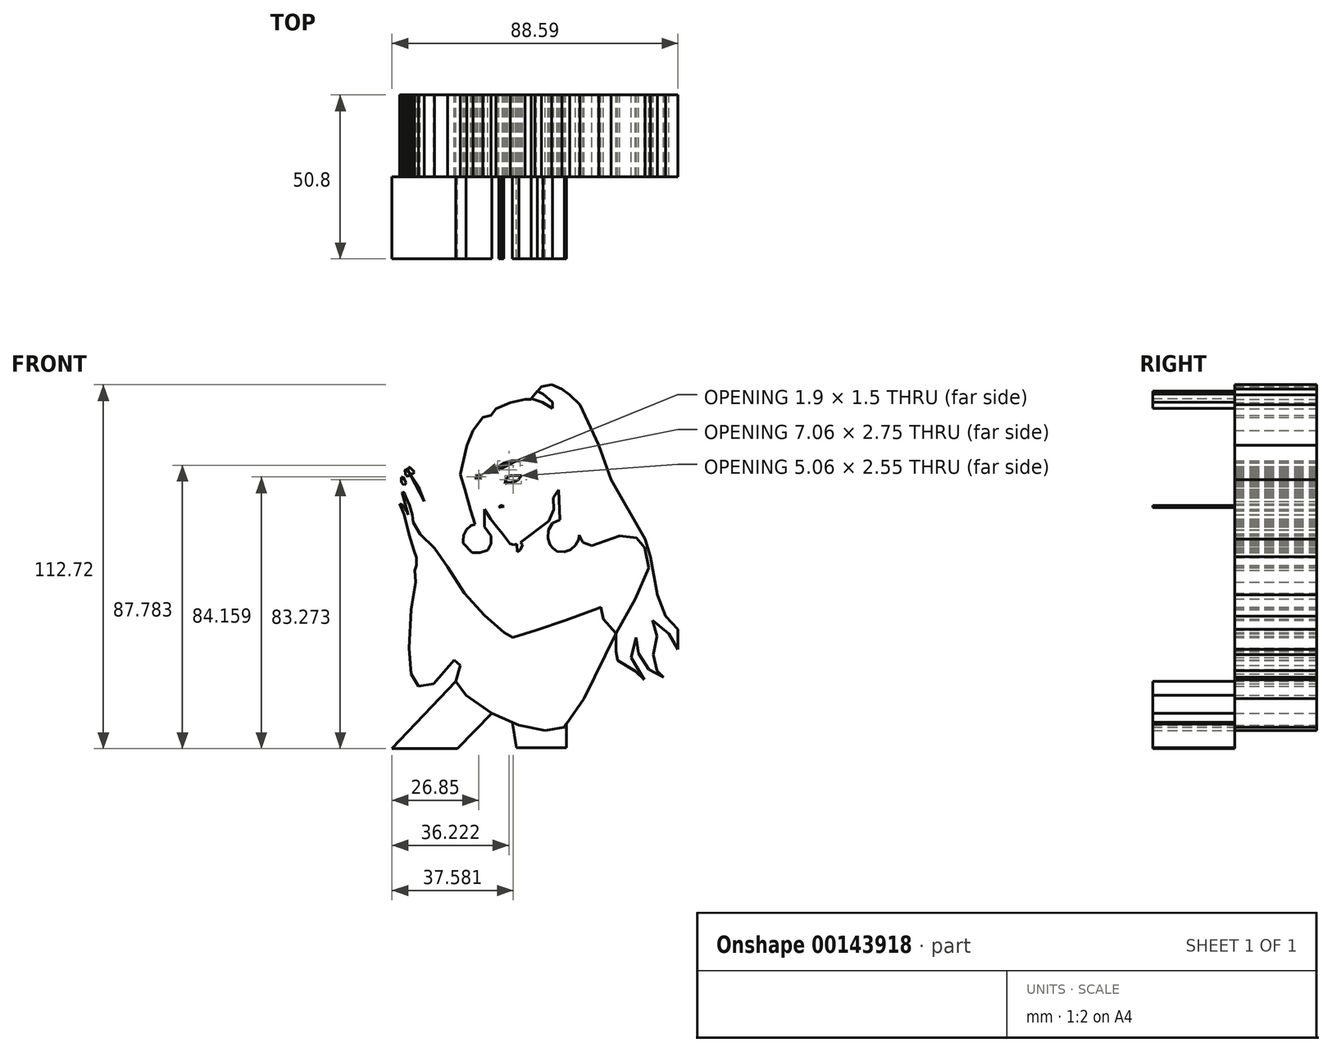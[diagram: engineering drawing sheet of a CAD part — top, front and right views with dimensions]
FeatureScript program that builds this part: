
annotation { "Feature Type Name" : "Feature", "Feature Type Description" : "" }
export const myFeature = defineFeature(function(context is Context, id is Id, definition is map)
    precondition{}
    {
        {
            var Q0;
            Q0=qCreatedBy(makeId("Front.planeOp"),FACE);
            var sketch = newSketch(context, id + "F0", { "sketchPlane" : qUnion([Q0])});
            skLineSegment(sketch, "E0", {"start": v(18.86, 2.45) * mm, "end": v(10.64, -3.42) * mm});
            skLineSegment(sketch, "E1", {"start": v(10.64, -3.42) * mm, "end": v(0.9, -7.18) * mm});
            skLineSegment(sketch, "E2", {"start": v(0.9, -7.18) * mm, "end": v(-4.27, -9.76) * mm});
            skLineSegment(sketch, "E3", {"start": v(-4.27, -9.76) * mm, "end": v(-10.84, -5.07) * mm});
            skLineSegment(sketch, "E4", {"start": v(-10.84, -5.07) * mm, "end": v(-17.53, 1.4) * mm});
            skLineSegment(sketch, "E5", {"start": v(-17.53, 1.4) * mm, "end": v(-24.1, 8.32) * mm});
            skLineSegment(sketch, "E6", {"start": v(-24.1, 8.32) * mm, "end": v(-25.63, 10.31) * mm});
            skLineSegment(sketch, "E7", {"start": v(-25.63, 10.31) * mm, "end": v(-25.63, 14.65) * mm});
            skLineSegment(sketch, "E8", {"start": v(-25.63, 14.65) * mm, "end": v(-27.16, 19.58) * mm});
            skLineSegment(sketch, "E9", {"start": v(-27.16, 19.58) * mm, "end": v(-28.21, 22.05) * mm});
            skLineSegment(sketch, "E10", {"start": v(-28.21, 22.05) * mm, "end": v(-28.21, 19.58) * mm});
            skLineSegment(sketch, "E11", {"start": v(-28.21, 19.58) * mm, "end": v(-27.07, 15.9) * mm});
            skLineSegment(sketch, "E12", {"start": v(-27.07, 15.9) * mm, "end": v(-28.21, 19.58) * mm});
            skLineSegment(sketch, "E13", {"start": v(-28.21, 19.58) * mm, "end": v(-32.09, 23.1) * mm});
            skLineSegment(sketch, "E14", {"start": v(-32.09, 23.1) * mm, "end": v(-36.08, 27.1) * mm});
            skLineSegment(sketch, "E15", {"start": v(30.24, -10.35) * mm, "end": v(20.73, -15.04) * mm});
            skLineSegment(sketch, "E16", {"start": v(20.73, -15.04) * mm, "end": v(10.64, -18.68) * mm});
            skLineSegment(sketch, "E17", {"start": v(10.64, -18.68) * mm, "end": v(1.7, -21.75) * mm});
            skLineSegment(sketch, "E18", {"start": v(1.7, -21.75) * mm, "end": v(-5.68, -24.05) * mm});
            skLineSegment(sketch, "E19", {"start": v(-5.68, -24.05) * mm, "end": v(-8.38, -22.56) * mm});
            skLineSegment(sketch, "E20", {"start": v(-8.38, -22.56) * mm, "end": v(-14.47, -17.16) * mm});
            skLineSegment(sketch, "E21", {"start": v(-14.47, -17.16) * mm, "end": v(-20.75, -10.33) * mm});
            skLineSegment(sketch, "E22", {"start": v(-20.75, -10.33) * mm, "end": v(-25.96, -2.28) * mm});
            skLineSegment(sketch, "E23", {"start": v(-25.96, -2.28) * mm, "end": v(-29.95, 3.6) * mm});
            skLineSegment(sketch, "E24", {"start": v(-29.95, 3.6) * mm, "end": v(-34.4, 7.97) * mm});
            skLineSegment(sketch, "E25", {"start": v(-34.4, 7.97) * mm, "end": v(-36.54, 11.65) * mm});
            skLineSegment(sketch, "E26", {"start": v(-28.55, 1.54) * mm, "end": v(-28.55, -3.51) * mm});
            skLineSegment(sketch, "E27", {"start": v(-28.55, -3.51) * mm, "end": v(-28.55, -14.12) * mm});
            skLineSegment(sketch, "E28", {"start": v(-28.55, -14.12) * mm, "end": v(-28.55, -20.51) * mm});
            skLineSegment(sketch, "E29", {"start": v(-28.55, -20.51) * mm, "end": v(-27.8, -29.5) * mm});
            skLineSegment(sketch, "E30", {"start": v(-28.55, -15.66) * mm, "end": v(-26.18, -10.8) * mm});
            skLineSegment(sketch, "E31", {"start": v(-26.18, -10.8) * mm, "end": v(-24.25, -4.93) * mm});
            skLineSegment(sketch, "E32", {"start": v(-40.74, 17.34) * mm, "end": v(-39.4, 14) * mm});
            skLineSegment(sketch, "E33", {"start": v(-39.4, 14) * mm, "end": v(-37.81, 7.82) * mm});
            skLineSegment(sketch, "E34", {"start": v(-37.81, 7.82) * mm, "end": v(-36.4, 2.8) * mm});
            skLineSegment(sketch, "E35", {"start": v(-36.4, 2.8) * mm, "end": v(-34.8, -1.46) * mm});
            skLineSegment(sketch, "E36", {"start": v(-35.6, 0.67) * mm, "end": v(-35.6, -1.68) * mm});
            skLineSegment(sketch, "E37", {"start": v(-35.6, -1.68) * mm, "end": v(-36.12, -3.2) * mm});
            skLineSegment(sketch, "E38", {"start": v(-36.12, -3.2) * mm, "end": v(-35.88, -6.96) * mm});
            skLineSegment(sketch, "E39", {"start": v(-35.88, -6.96) * mm, "end": v(-37.17, -15.36) * mm});
            skLineSegment(sketch, "E40", {"start": v(-37.17, -15.36) * mm, "end": v(-37.83, -27.34) * mm});
            skLineSegment(sketch, "E41", {"start": v(-37.83, -27.34) * mm, "end": v(-37.28, -35.34) * mm});
            skLineSegment(sketch, "E42", {"start": v(-37.28, -35.34) * mm, "end": v(-34.95, -39.15) * mm});
            skLineSegment(sketch, "E43", {"start": v(-34.95, -39.15) * mm, "end": v(-30.2, -38.45) * mm});
            skLineSegment(sketch, "E44", {"start": v(-30.2, -38.45) * mm, "end": v(-23.83, -31) * mm});
            skLineSegment(sketch, "E45", {"start": v(21.62, -14.6) * mm, "end": v(22.34, -18.4) * mm});
            skLineSegment(sketch, "E46", {"start": v(22.34, -18.4) * mm, "end": v(26.3, -22.78) * mm});
            skLineSegment(sketch, "E47", {"start": v(26.3, -22.78) * mm, "end": v(32.2, -12.1) * mm});
            skLineSegment(sketch, "E48", {"start": v(32.2, -12.1) * mm, "end": v(36.48, -2.41) * mm});
            skLineSegment(sketch, "E49", {"start": v(36.48, -2.41) * mm, "end": v(35.22, 3.73) * mm});
            skLineSegment(sketch, "E50", {"start": v(35.22, 3.73) * mm, "end": v(32.61, 6.76) * mm});
            skLineSegment(sketch, "E51", {"start": v(32.61, 6.76) * mm, "end": v(27.4, 7.44) * mm});
            skLineSegment(sketch, "E52", {"start": v(27.4, 7.44) * mm, "end": v(18.8, 4.4) * mm});
            skLineSegment(sketch, "E53", {"start": v(18.8, 4.4) * mm, "end": v(12.08, 2.39) * mm});
            skLineSegment(sketch, "E54", {"start": v(26.3, -22.78) * mm, "end": v(16.39, -43) * mm});
            skLineSegment(sketch, "E55", {"start": v(16.39, -43) * mm, "end": v(3.3, -37.77) * mm});
            skLineSegment(sketch, "E56", {"start": v(3.3, -37.77) * mm, "end": v(-6.56, -34.2) * mm});
            skLineSegment(sketch, "E57", {"start": v(-6.56, -34.2) * mm, "end": v(-15.48, -31) * mm});
            skLineSegment(sketch, "E58", {"start": v(16.39, -43) * mm, "end": v(10.24, -51.88) * mm});
            skLineSegment(sketch, "E59", {"start": v(10.24, -51.88) * mm, "end": v(4.3, -52.93) * mm});
            skLineSegment(sketch, "E60", {"start": v(4.3, -52.93) * mm, "end": v(-3.87, -51.22) * mm});
            skLineSegment(sketch, "E61", {"start": v(-3.87, -51.22) * mm, "end": v(-12.19, -47.52) * mm});
            skLineSegment(sketch, "E62", {"start": v(-12.19, -47.52) * mm, "end": v(-20.24, -41.98) * mm});
            skLineSegment(sketch, "E63", {"start": v(-20.24, -41.98) * mm, "end": v(-23.4, -37.63) * mm});
            skLineSegment(sketch, "E64", {"start": v(-23.4, -37.63) * mm, "end": v(-21.95, -32.74) * mm});
            skLineSegment(sketch, "E65", {"start": v(-23.4, -37.63) * mm, "end": v(-31.71, -46.2) * mm});
            skLineSegment(sketch, "E66", {"start": v(-31.71, -46.2) * mm, "end": v(-43.85, -58.08) * mm});
            skLineSegment(sketch, "E67", {"start": v(-12.19, -47.52) * mm, "end": v(-14.73, -51.21) * mm});
            skLineSegment(sketch, "E68", {"start": v(-14.73, -51.21) * mm, "end": v(-21.42, -56.76) * mm});
            skLineSegment(sketch, "E69", {"start": v(-21.42, -56.76) * mm, "end": v(-23, -58.34) * mm});
            skLineSegment(sketch, "E70", {"start": v(-5.82, -50.35) * mm, "end": v(-4.27, -55.3) * mm});
            skLineSegment(sketch, "E71", {"start": v(-4.27, -55.3) * mm, "end": v(-4.27, -58.6) * mm});
            skLineSegment(sketch, "E72", {"start": v(12.03, -49.29) * mm, "end": v(10.9, -58.6) * mm});
            skLineSegment(sketch, "E73", {"start": v(9.57, 20.9) * mm, "end": v(12, 14.2) * mm});
            skLineSegment(sketch, "E74", {"start": v(12, 14.2) * mm, "end": v(13.1, 10.76) * mm});
            skLineSegment(sketch, "E75", {"start": v(13.1, 10.76) * mm, "end": v(14.52, 8.33) * mm});
            skLineSegment(sketch, "E76", {"start": v(14.52, 8.33) * mm, "end": v(16.02, 5.4) * mm});
            skLineSegment(sketch, "E77", {"start": v(16.02, 5.4) * mm, "end": v(18.8, 4.4) * mm});
            skLineSegment(sketch, "E78", {"start": v(8.06, 21.15) * mm, "end": v(6.89, 19.23) * mm});
            skLineSegment(sketch, "E79", {"start": v(6.89, 19.23) * mm, "end": v(6.97, 15.54) * mm});
            skLineSegment(sketch, "E80", {"start": v(6.97, 15.54) * mm, "end": v(5.47, 12.02) * mm});
            skLineSegment(sketch, "E81", {"start": v(5.47, 12.02) * mm, "end": v(-3.33, 5.4) * mm});
            skLineSegment(sketch, "E82", {"start": v(-3.33, 5.4) * mm, "end": v(-4.4, 4.9) * mm});
            skLineSegment(sketch, "E83", {"start": v(-4.4, 4.9) * mm, "end": v(-5.5, 4.7) * mm});
            skLineSegment(sketch, "E84", {"start": v(-5.5, 4.7) * mm, "end": v(-6.68, 5.07) * mm});
            skLineSegment(sketch, "E85", {"start": v(-6.68, 5.07) * mm, "end": v(-7.41, 6.01) * mm});
            skLineSegment(sketch, "E86", {"start": v(-7.41, 6.01) * mm, "end": v(-8.89, 8.12) * mm});
            skLineSegment(sketch, "E87", {"start": v(-8.89, 8.12) * mm, "end": v(-10.62, 10.2) * mm});
            skLineSegment(sketch, "E88", {"start": v(-10.62, 10.2) * mm, "end": v(-12.65, 12.62) * mm});
            skLineSegment(sketch, "E89", {"start": v(-12.65, 12.62) * mm, "end": v(-14.56, 15.73) * mm});
            skLineSegment(sketch, "E90", {"start": v(-14.56, 15.73) * mm, "end": v(-15.45, 18.58) * mm});
            skLineSegment(sketch, "E91", {"start": v(-15.45, 18.58) * mm, "end": v(-15.45, 20.85) * mm});
            skLineSegment(sketch, "E92", {"start": v(-15.45, 20.85) * mm, "end": v(-16.92, 23.97) * mm});
            skLineSegment(sketch, "E93", {"start": v(-11.01, 36.98) * mm, "end": v(-13.12, 36.98) * mm});
            skLineSegment(sketch, "E94", {"start": v(-13.12, 36.98) * mm, "end": v(-14.77, 35.8) * mm});
            skLineSegment(sketch, "E95", {"start": v(-14.77, 35.8) * mm, "end": v(-15.87, 34.42) * mm});
            skLineSegment(sketch, "E96", {"start": v(-15.87, 34.42) * mm, "end": v(-16.55, 31.4) * mm});
            skLineSegment(sketch, "E97", {"start": v(-16.55, 31.4) * mm, "end": v(-17.24, 25.9) * mm});
            skLineSegment(sketch, "E98", {"start": v(-17.24, 25.9) * mm, "end": v(-17.24, 20.18) * mm});
            skLineSegment(sketch, "E99", {"start": v(-17.24, 20.18) * mm, "end": v(-16.74, 13.5) * mm});
            skLineSegment(sketch, "E100", {"start": v(-8.31, 37.21) * mm, "end": v(-5.89, 38.45) * mm});
            skLineSegment(sketch, "E101", {"start": v(-5.89, 38.45) * mm, "end": v(-2.73, 36.39) * mm});
            skLineSegment(sketch, "E102", {"start": v(-2.73, 36.39) * mm, "end": v(0.02, 32.45) * mm});
            skLineSegment(sketch, "E103", {"start": v(0.02, 32.45) * mm, "end": v(2.08, 27.42) * mm});
            skLineSegment(sketch, "E104", {"start": v(2.08, 27.42) * mm, "end": v(3, 21.92) * mm});
            skLineSegment(sketch, "E105", {"start": v(3, 21.92) * mm, "end": v(2.4, 17.34) * mm});
            skLineSegment(sketch, "E106", {"start": v(2.4, 17.34) * mm, "end": v(1.94, 13.45) * mm});
            skLineSegment(sketch, "E107", {"start": v(-3.33, 5.4) * mm, "end": v(-2.71, 4.58) * mm});
            skLineSegment(sketch, "E108", {"start": v(-2.71, 4.58) * mm, "end": v(-3.43, 3.03) * mm});
            skLineSegment(sketch, "E109", {"start": v(-3.43, 3.03) * mm, "end": v(-4.38, 2.5) * mm});
            skLineSegment(sketch, "E110", {"start": v(-4.38, 2.5) * mm, "end": v(-4.4, 4.9) * mm});
            skLineSegment(sketch, "E111", {"start": v(-4.38, 2.5) * mm, "end": v(-4.38, -0.87) * mm});
            skLineSegment(sketch, "E112", {"start": v(-4.38, -0.87) * mm, "end": v(-3.4, -4.34) * mm});
            skLineSegment(sketch, "E113", {"start": v(-3.4, -4.34) * mm, "end": v(-3.13, -6.75) * mm});
            skLineSegment(sketch, "E114", {"start": v(-23.07, -6.75) * mm, "end": v(-24.38, -11.78) * mm});
            skLineSegment(sketch, "E115", {"start": v(-24.38, -11.78) * mm, "end": v(-26.14, -16.59) * mm});
            skLineSegment(sketch, "E116", {"start": v(-26.14, -16.59) * mm, "end": v(-26.67, -23) * mm});
            skLineSegment(sketch, "E117", {"start": v(-26.67, -23) * mm, "end": v(-25.45, -27.97) * mm});
            skLineSegment(sketch, "E118", {"start": v(-25.45, -27.97) * mm, "end": v(-23.83, -31) * mm});
            skLineSegment(sketch, "E119", {"start": v(-23.83, -31) * mm, "end": v(-21.95, -32.74) * mm});
            skLineSegment(sketch, "E120", {"start": v(-21.95, -32.74) * mm, "end": v(-19.65, -38.05) * mm});
            skLineSegment(sketch, "E121", {"start": v(-19.65, -38.05) * mm, "end": v(-19.95, -39.04) * mm});
            skLineSegment(sketch, "E122", {"start": v(-19.95, -39.04) * mm, "end": v(-17.2, -36.06) * mm});
            skLineSegment(sketch, "E123", {"start": v(-17.2, -36.06) * mm, "end": v(-16.06, -33) * mm});
            skLineSegment(sketch, "E124", {"start": v(-16.06, -33) * mm, "end": v(-15.48, -31) * mm});
            skLineSegment(sketch, "E125", {"start": v(-15.48, -31) * mm, "end": v(-15.48, -27.2) * mm});
            skLineSegment(sketch, "E126", {"start": v(-15.48, -27.2) * mm, "end": v(-14.6, -23.46) * mm});
            skLineSegment(sketch, "E127", {"start": v(-14.6, -23.46) * mm, "end": v(-14.53, -22.32) * mm});
            skLineSegment(sketch, "E128", {"start": v(-14.53, -22.32) * mm, "end": v(-14.94, -16.64) * mm});
            skLineSegment(sketch, "E129", {"start": v(2.82, 38.96) * mm, "end": v(5.72, 34.85) * mm});
            skLineSegment(sketch, "E130", {"start": v(5.72, 34.85) * mm, "end": v(5.78, 30.48) * mm});
            skLineSegment(sketch, "E131", {"start": v(5.78, 30.48) * mm, "end": v(5.11, 23.15) * mm});
            skLineSegment(sketch, "E132", {"start": v(5.11, 23.15) * mm, "end": v(4.5, 17.96) * mm});
            skLineSegment(sketch, "E133", {"start": v(4.5, 17.96) * mm, "end": v(5.47, 12.02) * mm});
            skLineSegment(sketch, "E134", {"start": v(5.45, 26.81) * mm, "end": v(8.06, 25.9) * mm});
            skLineSegment(sketch, "E135", {"start": v(8.06, 25.9) * mm, "end": v(11.81, 25.9) * mm});
            skLineSegment(sketch, "E136", {"start": v(11.81, 25.9) * mm, "end": v(11.81, 28.47) * mm});
            skLineSegment(sketch, "E137", {"start": v(11.81, 28.47) * mm, "end": v(13.33, 31.38) * mm});
            skLineSegment(sketch, "E138", {"start": v(13.33, 31.38) * mm, "end": v(13.33, 36.87) * mm});
            skLineSegment(sketch, "E139", {"start": v(13.33, 36.87) * mm, "end": v(15.58, 32.5) * mm});
            skLineSegment(sketch, "E140", {"start": v(15.58, 32.5) * mm, "end": v(17.43, 29.6) * mm});
            skLineSegment(sketch, "E141", {"start": v(-6.78, 43.7) * mm, "end": v(-9.85, 45.56) * mm});
            skLineSegment(sketch, "E142", {"start": v(-9.85, 45.56) * mm, "end": v(-14.96, 44.07) * mm});
            skLineSegment(sketch, "E143", {"start": v(-14.96, 44.07) * mm, "end": v(-18.02, 40.08) * mm});
            skLineSegment(sketch, "E144", {"start": v(-18.02, 40.08) * mm, "end": v(-19.97, 35.34) * mm});
            skLineSegment(sketch, "E145", {"start": v(-19.97, 35.34) * mm, "end": v(-22.02, 26.52) * mm});
            skLineSegment(sketch, "E146", {"start": v(-22.02, 26.52) * mm, "end": v(-20.62, 21.96) * mm});
            skLineSegment(sketch, "E147", {"start": v(-20.62, 21.96) * mm, "end": v(-18.77, 15.46) * mm});
            skLineSegment(sketch, "E148", {"start": v(-18.77, 15.46) * mm, "end": v(-15.24, 3.76) * mm});
            skLineSegment(sketch, "E149", {"start": v(-15.24, 3.76) * mm, "end": v(-16.74, 13.5) * mm});
            skLineSegment(sketch, "E150", {"start": v(15.14, 48.07) * mm, "end": v(20.9, 35.53) * mm});
            skLineSegment(sketch, "E151", {"start": v(20.9, 35.53) * mm, "end": v(24.8, 24.84) * mm});
            skLineSegment(sketch, "E152", {"start": v(24.8, 24.84) * mm, "end": v(35.3, 6.45) * mm});
            skLineSegment(sketch, "E153", {"start": v(35.3, 6.45) * mm, "end": v(36.88, 0.97) * mm});
            skLineSegment(sketch, "E154", {"start": v(36.88, 0.97) * mm, "end": v(39.1, -10.83) * mm});
            skLineSegment(sketch, "E155", {"start": v(37.6, -18.7) * mm, "end": v(42.64, -22.92) * mm});
            skLineSegment(sketch, "E156", {"start": v(42.64, -22.92) * mm, "end": v(45.45, -27.72) * mm});
            skLineSegment(sketch, "E157", {"start": v(45.45, -27.72) * mm, "end": v(45.45, -21.51) * mm});
            skLineSegment(sketch, "E158", {"start": v(45.45, -21.51) * mm, "end": v(41.58, -17.41) * mm});
            skLineSegment(sketch, "E159", {"start": v(41.58, -17.41) * mm, "end": v(39.1, -10.83) * mm});
            skLineSegment(sketch, "E160", {"start": v(37.6, -18.7) * mm, "end": v(39, -23.74) * mm});
            skLineSegment(sketch, "E161", {"start": v(39, -23.74) * mm, "end": v(37.84, -29.36) * mm});
            skLineSegment(sketch, "E162", {"start": v(37.84, -29.36) * mm, "end": v(39, -34.4) * mm});
            skLineSegment(sketch, "E163", {"start": v(39, -34.4) * mm, "end": v(41, -36.38) * mm});
            skLineSegment(sketch, "E164", {"start": v(41, -36.38) * mm, "end": v(36.43, -33.92) * mm});
            skLineSegment(sketch, "E165", {"start": v(36.43, -33.92) * mm, "end": v(33.27, -29) * mm});
            skLineSegment(sketch, "E166", {"start": v(33.27, -29) * mm, "end": v(32.45, -24.09) * mm});
            skLineSegment(sketch, "E167", {"start": v(32.45, -24.09) * mm, "end": v(32.1, -18.23) * mm});
            skLineSegment(sketch, "E168", {"start": v(32.1, -18.23) * mm, "end": v(31.98, -15.54) * mm});
            skLineSegment(sketch, "E169", {"start": v(37.6, -18.7) * mm, "end": v(35.03, -15.42) * mm});
            skLineSegment(sketch, "E170", {"start": v(35.03, -15.42) * mm, "end": v(34.32, -11.8) * mm});
            skLineSegment(sketch, "E171", {"start": v(26.3, -22.78) * mm, "end": v(26.3, -28.42) * mm});
            skLineSegment(sketch, "E172", {"start": v(26.3, -28.42) * mm, "end": v(26.83, -31.23) * mm});
            skLineSegment(sketch, "E173", {"start": v(26.83, -31.23) * mm, "end": v(32.22, -34.51) * mm});
            skLineSegment(sketch, "E174", {"start": v(32.22, -34.51) * mm, "end": v(35.03, -37.09) * mm});
            skLineSegment(sketch, "E175", {"start": v(35.03, -37.09) * mm, "end": v(30.93, -30.3) * mm});
            skLineSegment(sketch, "E176", {"start": v(30.93, -30.3) * mm, "end": v(32.45, -24.09) * mm});
            skLineSegment(sketch, "E177", {"start": v(2.17, 49.78) * mm, "end": v(-1.89, 49.78) * mm});
            skLineSegment(sketch, "E178", {"start": v(-1.89, 49.78) * mm, "end": v(-6.43, 48.73) * mm});
            skLineSegment(sketch, "E179", {"start": v(-6.43, 48.73) * mm, "end": v(-10.97, 46.78) * mm});
            skLineSegment(sketch, "E180", {"start": v(-10.97, 46.78) * mm, "end": v(-12.4, 44.82) * mm});
            skLineSegment(sketch, "E181", {"start": v(2.17, 49.78) * mm, "end": v(6.06, 46.78) * mm});
            skLineSegment(sketch, "E182", {"start": v(6.06, 46.78) * mm, "end": v(11, 42.32) * mm});
            skLineSegment(sketch, "E183", {"start": v(11, 42.32) * mm, "end": v(13.33, 36.87) * mm});
            skLineSegment(sketch, "E184", {"start": v(0, 49.78) * mm, "end": v(1.08, 51.18) * mm});
            skLineSegment(sketch, "E185", {"start": v(1.08, 51.18) * mm, "end": v(3.46, 51.4) * mm});
            skLineSegment(sketch, "E186", {"start": v(3.46, 51.4) * mm, "end": v(6.14, 49.7) * mm});
            skLineSegment(sketch, "E187", {"start": v(6.14, 49.7) * mm, "end": v(6.55, 48.57) * mm});
            skLineSegment(sketch, "E188", {"start": v(6.55, 48.57) * mm, "end": v(5.98, 47.19) * mm});
            skLineSegment(sketch, "E189", {"start": v(5.98, 47.19) * mm, "end": v(6.06, 46.78) * mm});
            skLineSegment(sketch, "E190", {"start": v(1.08, 51.18) * mm, "end": v(3.14, 53.6) * mm});
            skLineSegment(sketch, "E191", {"start": v(3.14, 53.6) * mm, "end": v(6.38, 54.25) * mm});
            skLineSegment(sketch, "E192", {"start": v(6.38, 54.25) * mm, "end": v(9.47, 52.95) * mm});
            skLineSegment(sketch, "E193", {"start": v(9.47, 52.95) * mm, "end": v(11.9, 51.08) * mm});
            skLineSegment(sketch, "E194", {"start": v(11.9, 51.08) * mm, "end": v(15.14, 48.07) * mm});
            skLineSegment(sketch, "E195", {"start": v(13.1, 10.76) * mm, "end": v(10.92, 12.02) * mm});
            skLineSegment(sketch, "E196", {"start": v(10.92, 12.02) * mm, "end": v(8.88, 12.33) * mm});
            skLineSegment(sketch, "E197", {"start": v(8.88, 12.33) * mm, "end": v(6.64, 11.41) * mm});
            skLineSegment(sketch, "E198", {"start": v(6.64, 11.41) * mm, "end": v(5.27, 9.17) * mm});
            skLineSegment(sketch, "E199", {"start": v(5.27, 9.17) * mm, "end": v(5.22, 6.72) * mm});
            skLineSegment(sketch, "E200", {"start": v(5.22, 6.72) * mm, "end": v(5.87, 4.58) * mm});
            skLineSegment(sketch, "E201", {"start": v(5.87, 4.58) * mm, "end": v(6.69, 3.58) * mm});
            skLineSegment(sketch, "E202", {"start": v(6.69, 3.58) * mm, "end": v(7.99, 2.57) * mm});
            skLineSegment(sketch, "E203", {"start": v(7.99, 2.57) * mm, "end": v(10.31, 2.51) * mm});
            skLineSegment(sketch, "E204", {"start": v(10.31, 2.51) * mm, "end": v(12.17, 3.07) * mm});
            skLineSegment(sketch, "E205", {"start": v(12.17, 3.07) * mm, "end": v(13.7, 4.52) * mm});
            skLineSegment(sketch, "E206", {"start": v(13.7, 4.52) * mm, "end": v(14.67, 6.29) * mm});
            skLineSegment(sketch, "E207", {"start": v(14.67, 6.29) * mm, "end": v(14.86, 7.67) * mm});
            skLineSegment(sketch, "E208", {"start": v(-17.42, 10.98) * mm, "end": v(-18.69, 10.6) * mm});
            skLineSegment(sketch, "E209", {"start": v(-18.69, 10.6) * mm, "end": v(-20.03, 9.28) * mm});
            skLineSegment(sketch, "E210", {"start": v(-20.03, 9.28) * mm, "end": v(-20.93, 7.59) * mm});
            skLineSegment(sketch, "E211", {"start": v(-20.93, 7.59) * mm, "end": v(-21.13, 5.9) * mm});
            skLineSegment(sketch, "E212", {"start": v(-21.13, 5.9) * mm, "end": v(-21.13, 5.18) * mm});
            skLineSegment(sketch, "E213", {"start": v(-21.13, 5.18) * mm, "end": v(-21, 4.96) * mm});
            skLineSegment(sketch, "E214", {"start": v(-16.34, 10.96) * mm, "end": v(-14.52, 10.2) * mm});
            skLineSegment(sketch, "E215", {"start": v(-14.52, 10.2) * mm, "end": v(-12.5, 7.4) * mm});
            skLineSegment(sketch, "E216", {"start": v(-12.5, 7.4) * mm, "end": v(-12.5, 4.98) * mm});
            skLineSegment(sketch, "E217", {"start": v(-12.5, 4.98) * mm, "end": v(-13.5, 3) * mm});
            skLineSegment(sketch, "E218", {"start": v(-13.5, 3) * mm, "end": v(-15.88, 2.22) * mm});
            skLineSegment(sketch, "E219", {"start": v(-15.88, 2.22) * mm, "end": v(-18.32, 2.22) * mm});
            skLineSegment(sketch, "E220", {"start": v(-29.84, 18.18) * mm, "end": v(-32.99, 23.1) * mm});
            skLineSegment(sketch, "E221", {"start": v(-32.99, 23.1) * mm, "end": v(-36.08, 27.1) * mm});
            skLineSegment(sketch, "E222", {"start": v(-33.15, 18.1) * mm, "end": v(-34.98, 22.64) * mm});
            skLineSegment(sketch, "E223", {"start": v(-34.98, 22.64) * mm, "end": v(-37.77, 26.82) * mm});
            skLineSegment(sketch, "E224", {"start": v(-37.77, 26.82) * mm, "end": v(-35.98, 23.43) * mm});
            skLineSegment(sketch, "E225", {"start": v(-35.98, 23.43) * mm, "end": v(-33.15, 18.1) * mm});
            skLineSegment(sketch, "E226", {"start": v(-35.3, 16.5) * mm, "end": v(-38.8, 26.1) * mm});
            skLineSegment(sketch, "E227", {"start": v(-38.73, 23.83) * mm, "end": v(-35.3, 16.5) * mm});
            skLineSegment(sketch, "E228", {"start": v(-40, 23.11) * mm, "end": v(-38.88, 19.45) * mm});
            skLineSegment(sketch, "E229", {"start": v(-38.88, 19.45) * mm, "end": v(-37.73, 16.98) * mm});
            skLineSegment(sketch, "E230", {"start": v(-37.73, 16.98) * mm, "end": v(-36.85, 13.95) * mm});
            skLineSegment(sketch, "E231", {"start": v(-36.85, 13.95) * mm, "end": v(-36.54, 11.65) * mm});
            skLineSegment(sketch, "E232", {"start": v(-40.74, 17.34) * mm, "end": v(-39.8, 16.95) * mm});
            skLineSegment(sketch, "E233", {"start": v(-39.8, 16.95) * mm, "end": v(-38.62, 15.12) * mm});
            skLineSegment(sketch, "E234", {"start": v(-38.62, 15.12) * mm, "end": v(-37.04, 11.57) * mm});
            skLineSegment(sketch, "E235", {"start": v(-37.04, 11.57) * mm, "end": v(-36.45, 9.98) * mm});
            skLineSegment(sketch, "E236", {"start": v(-38.1, 13.96) * mm, "end": v(-39.76, 19.82) * mm});
            skLineSegment(sketch, "E237", {"start": v(-39.76, 19.82) * mm, "end": v(-40, 20.73) * mm});
            skLineSegment(sketch, "E238", {"start": v(-40, 20.73) * mm, "end": v(-39.86, 20.99) * mm});
            skLineSegment(sketch, "E239", {"start": v(-39.86, 20.99) * mm, "end": v(-39.5, 20.87) * mm});
            skLineSegment(sketch, "E240", {"start": v(-39.5, 20.87) * mm, "end": v(-39.28, 20.68) * mm});
            skLineSegment(sketch, "E241", {"start": v(-39.28, 20.68) * mm, "end": v(-39.07, 20.07) * mm});
            skLineSegment(sketch, "E242", {"start": v(-40, 23.11) * mm, "end": v(-40.27, 24.27) * mm});
            skLineSegment(sketch, "E243", {"start": v(-40.27, 24.27) * mm, "end": v(-40.3, 25.29) * mm});
            skLineSegment(sketch, "E244", {"start": v(-40.3, 25.29) * mm, "end": v(-40.15, 25.57) * mm});
            skLineSegment(sketch, "E245", {"start": v(-40.15, 25.57) * mm, "end": v(-39.9, 25.69) * mm});
            skLineSegment(sketch, "E246", {"start": v(-39.9, 25.69) * mm, "end": v(-39.6, 25.44) * mm});
            skLineSegment(sketch, "E247", {"start": v(-39.6, 25.44) * mm, "end": v(-39.24, 24.86) * mm});
            skLineSegment(sketch, "E248", {"start": v(-39.24, 24.86) * mm, "end": v(-38.97, 24.36) * mm});
            skLineSegment(sketch, "E249", {"start": v(-38.97, 24.36) * mm, "end": v(-38.8, 24.02) * mm});
            skLineSegment(sketch, "E250", {"start": v(-38.8, 24.02) * mm, "end": v(-38.73, 23.83) * mm});
            skLineSegment(sketch, "E251", {"start": v(-40.18, 23.91) * mm, "end": v(-39.79, 23.38) * mm});
            skLineSegment(sketch, "E252", {"start": v(-39.79, 23.38) * mm, "end": v(-39.39, 23.24) * mm});
            skLineSegment(sketch, "E253", {"start": v(-39.39, 23.24) * mm, "end": v(-38.96, 23.49) * mm});
            skLineSegment(sketch, "E254", {"start": v(-38.96, 23.49) * mm, "end": v(-38.92, 23.93) * mm});
            skLineSegment(sketch, "E255", {"start": v(-38.92, 23.93) * mm, "end": v(-38.97, 24.36) * mm});
            skLineSegment(sketch, "E256", {"start": v(-38.87, 28.1) * mm, "end": v(-39.12, 27.68) * mm});
            skLineSegment(sketch, "E257", {"start": v(-39.12, 27.68) * mm, "end": v(-39.03, 26.77) * mm});
            skLineSegment(sketch, "E258", {"start": v(-39.03, 26.77) * mm, "end": v(-38.8, 26.1) * mm});
            skLineSegment(sketch, "E259", {"start": v(-38.8, 26.1) * mm, "end": v(-38.48, 25.95) * mm});
            skLineSegment(sketch, "E260", {"start": v(-38.48, 25.95) * mm, "end": v(-38.1, 25.95) * mm});
            skLineSegment(sketch, "E261", {"start": v(-38.1, 25.95) * mm, "end": v(-37.9, 26.1) * mm});
            skLineSegment(sketch, "E262", {"start": v(-37.9, 26.1) * mm, "end": v(-37.75, 26.4) * mm});
            skLineSegment(sketch, "E263", {"start": v(-37.75, 26.4) * mm, "end": v(-37.77, 26.82) * mm});
            skLineSegment(sketch, "E264", {"start": v(-38.87, 28.1) * mm, "end": v(-38.64, 27.97) * mm});
            skLineSegment(sketch, "E265", {"start": v(-38.64, 27.97) * mm, "end": v(-38.3, 27.66) * mm});
            skLineSegment(sketch, "E266", {"start": v(-38.3, 27.66) * mm, "end": v(-38.06, 27.3) * mm});
            skLineSegment(sketch, "E267", {"start": v(-38.06, 27.3) * mm, "end": v(-37.77, 26.82) * mm});
            skLineSegment(sketch, "E268", {"start": v(-38.02, 28.58) * mm, "end": v(-38.12, 28.08) * mm});
            skLineSegment(sketch, "E269", {"start": v(-38.12, 28.08) * mm, "end": v(-37.94, 27.4) * mm});
            skLineSegment(sketch, "E270", {"start": v(-37.94, 27.4) * mm, "end": v(-37.63, 26.9) * mm});
            skLineSegment(sketch, "E271", {"start": v(-37.63, 26.9) * mm, "end": v(-37.26, 26.64) * mm});
            skLineSegment(sketch, "E272", {"start": v(-37.26, 26.64) * mm, "end": v(-36.74, 26.59) * mm});
            skLineSegment(sketch, "E273", {"start": v(-36.74, 26.59) * mm, "end": v(-36.41, 26.8) * mm});
            skLineSegment(sketch, "E274", {"start": v(-36.41, 26.8) * mm, "end": v(-36.21, 27.19) * mm});
            skLineSegment(sketch, "E275", {"start": v(-36.21, 27.19) * mm, "end": v(-36.93, 28.03) * mm});
            skLineSegment(sketch, "E276", {"start": v(-36.93, 28.03) * mm, "end": v(-37.63, 28.65) * mm});
            skLineSegment(sketch, "E277", {"start": v(-37.63, 28.65) * mm, "end": v(-37.94, 28.67) * mm});
            skLineSegment(sketch, "E278", {"start": v(-37.94, 28.67) * mm, "end": v(-38.02, 28.58) * mm});
            skLineSegment(sketch, "E279", {"start": v(-36.21, 27.19) * mm, "end": v(-36.08, 27.1) * mm});
            skLineSegment(sketch, "E280", {"start": v(-16.92, 23.97) * mm, "end": v(-17.24, 25.9) * mm});
            skLineSegment(sketch, "E281", {"start": v(1.94, 13.45) * mm, "end": v(4.5, 17.96) * mm});
            skLineSegment(sketch, "E282", {"start": v(11.81, 25.9) * mm, "end": v(10.84, 23.67) * mm});
            skLineSegment(sketch, "E283", {"start": v(10.84, 23.67) * mm, "end": v(9.89, 21.28) * mm});
            skLineSegment(sketch, "E284", {"start": v(9.89, 21.28) * mm, "end": v(9.57, 20.9) * mm});
            skLineSegment(sketch, "E285", {"start": v(9.24, 21.59) * mm, "end": v(8.98, 21.9) * mm});
            skLineSegment(sketch, "E286", {"start": v(8.98, 21.9) * mm, "end": v(8.47, 21.63) * mm});
            skLineSegment(sketch, "E287", {"start": v(8.47, 21.63) * mm, "end": v(8.88, 12.33) * mm});
            skLineSegment(sketch, "E288", {"start": v(9.24, 21.59) * mm, "end": v(8.88, 12.33) * mm});
            skLineSegment(sketch, "E289", {"start": v(9.57, 20.9) * mm, "end": v(9.22, 21.19) * mm});
            skLineSegment(sketch, "E290", {"start": v(9.22, 21.19) * mm, "end": v(9.24, 21.59) * mm});
            skLineSegment(sketch, "E291", {"start": v(8.06, 21.15) * mm, "end": v(8.47, 21.63) * mm});
            skLineSegment(sketch, "E292", {"start": v(-14.52, 10.2) * mm, "end": v(-14.56, 15.73) * mm});
            skLineSegment(sketch, "E293", {"start": v(-14.43, 10.26) * mm, "end": v(-14.12, 15.02) * mm});
            skLineSegment(sketch, "E294", {"start": v(-14.12, 15.02) * mm, "end": v(-14.56, 15.73) * mm});
            skLineSegment(sketch, "E295", {"start": v(-10.1, 27.94) * mm, "end": v(-8.06, 28.86) * mm});
            skLineSegment(sketch, "E296", {"start": v(-8.06, 28.86) * mm, "end": v(-4.9, 30.55) * mm});
            skLineSegment(sketch, "E297", {"start": v(-4.9, 30.55) * mm, "end": v(-3.39, 30.69) * mm});
            skLineSegment(sketch, "E298", {"start": v(-3.39, 30.69) * mm, "end": v(-6.11, 30.69) * mm});
            skLineSegment(sketch, "E299", {"start": v(-6.11, 30.69) * mm, "end": v(-8.21, 29.98) * mm});
            skLineSegment(sketch, "E300", {"start": v(-8.21, 29.98) * mm, "end": v(-10.31, 28.76) * mm});
            skLineSegment(sketch, "E301", {"start": v(-10.31, 28.76) * mm, "end": v(-10.45, 28.33) * mm});
            skLineSegment(sketch, "E302", {"start": v(-10.45, 28.33) * mm, "end": v(-10.1, 27.94) * mm});
            skLineSegment(sketch, "E303", {"start": v(-17.08, 24.94) * mm, "end": v(-16.47, 25.48) * mm});
            skLineSegment(sketch, "E304", {"start": v(-16.47, 25.48) * mm, "end": v(-15.43, 25.62) * mm});
            skLineSegment(sketch, "E305", {"start": v(-15.43, 25.62) * mm, "end": v(-15.34, 25.93) * mm});
            skLineSegment(sketch, "E306", {"start": v(-15.34, 25.93) * mm, "end": v(-15.72, 26.44) * mm});
            skLineSegment(sketch, "E307", {"start": v(-15.72, 26.44) * mm, "end": v(-16.56, 26.24) * mm});
            skLineSegment(sketch, "E308", {"start": v(-16.56, 26.24) * mm, "end": v(-17.24, 25.9) * mm});
            skLineSegment(sketch, "E309", {"start": v(-13.5, 24.48) * mm, "end": v(-12.32, 23.67) * mm});
            skLineSegment(sketch, "E310", {"start": v(-12.32, 23.67) * mm, "end": v(-12.45, 20) * mm});
            skLineSegment(sketch, "E311", {"start": v(-12.45, 20) * mm, "end": v(-12.66, 18.45) * mm});
            skLineSegment(sketch, "E312", {"start": v(-12.66, 18.45) * mm, "end": v(-12.85, 17.55) * mm});
            skLineSegment(sketch, "E313", {"start": v(-12.85, 17.55) * mm, "end": v(-12.66, 16.63) * mm});
            skLineSegment(sketch, "E314", {"start": v(-12.66, 16.63) * mm, "end": v(-12, 15.73) * mm});
            skLineSegment(sketch, "E315", {"start": v(-12, 15.73) * mm, "end": v(-11.12, 15.5) * mm});
            skLineSegment(sketch, "E316", {"start": v(-11.12, 15.5) * mm, "end": v(-10.4, 15.5) * mm});
            skLineSegment(sketch, "E317", {"start": v(-7.81, 16.23) * mm, "end": v(-7.35, 16.86) * mm});
            skLineSegment(sketch, "E318", {"start": v(-7.35, 16.86) * mm, "end": v(-7.72, 17.76) * mm});
            skLineSegment(sketch, "E319", {"start": v(-10.04, 16.14) * mm, "end": v(-9.39, 16.43) * mm});
            skLineSegment(sketch, "E320", {"start": v(-9.39, 16.43) * mm, "end": v(-8.73, 16.31) * mm});
            skLineSegment(sketch, "E321", {"start": v(-8.73, 16.31) * mm, "end": v(-8.5, 16.55) * mm});
            skLineSegment(sketch, "E322", {"start": v(-8.5, 16.55) * mm, "end": v(-8.65, 16.78) * mm});
            skLineSegment(sketch, "E323", {"start": v(-8.65, 16.78) * mm, "end": v(-9.3, 16.86) * mm});
            skLineSegment(sketch, "E324", {"start": v(-9.3, 16.86) * mm, "end": v(-9.93, 16.46) * mm});
            skLineSegment(sketch, "E325", {"start": v(-9.93, 16.46) * mm, "end": v(-10, 16.3) * mm});
            skLineSegment(sketch, "E326", {"start": v(-10, 16.3) * mm, "end": v(-10.05, 16.15) * mm});
            skLineSegment(sketch, "E327", {"start": v(-10.05, 16.15) * mm, "end": v(-10, 16.3) * mm});
            skLineSegment(sketch, "E328", {"start": v(-8.09, 23.53) * mm, "end": v(-7.51, 23.9) * mm});
            skLineSegment(sketch, "E329", {"start": v(-7.51, 23.9) * mm, "end": v(-6.48, 23.95) * mm});
            skLineSegment(sketch, "E330", {"start": v(-6.48, 23.95) * mm, "end": v(-4.85, 24.3) * mm});
            skLineSegment(sketch, "E331", {"start": v(-4.85, 24.3) * mm, "end": v(-3.93, 24.83) * mm});
            skLineSegment(sketch, "E332", {"start": v(-3.93, 24.83) * mm, "end": v(-3.03, 26.08) * mm});
            skLineSegment(sketch, "E333", {"start": v(-3.03, 26.08) * mm, "end": v(-4.11, 26.08) * mm});
            skLineSegment(sketch, "E334", {"start": v(-4.11, 26.08) * mm, "end": v(-6.35, 26.08) * mm});
            skLineSegment(sketch, "E335", {"start": v(-6.35, 26.08) * mm, "end": v(-7.23, 25.66) * mm});
            skLineSegment(sketch, "E336", {"start": v(-7.23, 25.66) * mm, "end": v(-7.87, 24.78) * mm});
            skLineSegment(sketch, "E337", {"start": v(-7.87, 24.78) * mm, "end": v(-8.09, 23.53) * mm});
            skLineSegment(sketch, "E338", {"start": v(-6, 26.08) * mm, "end": v(-6.37, 25.46) * mm});
            skLineSegment(sketch, "E339", {"start": v(-6.37, 25.46) * mm, "end": v(-6.24, 24.77) * mm});
            skLineSegment(sketch, "E340", {"start": v(-6.24, 24.77) * mm, "end": v(-5.5, 24.46) * mm});
            skLineSegment(sketch, "E341", {"start": v(-5.5, 24.46) * mm, "end": v(-4.83, 24.56) * mm});
            skLineSegment(sketch, "E342", {"start": v(-4.83, 24.56) * mm, "end": v(-4.26, 25.28) * mm});
            skLineSegment(sketch, "E343", {"start": v(-4.26, 25.28) * mm, "end": v(-4.4, 25.9) * mm});
            skLineSegment(sketch, "E344", {"start": v(-4.4, 25.9) * mm, "end": v(-4.57, 26.07) * mm});
            skLineSegment(sketch, "E345", {"start": v(-4.57, 26.07) * mm, "end": v(-4.11, 26.08) * mm});
            skSolve(sketch);
        }
        {
            var Q0;
            Q0 = qSketchRegion(id + "F0", true);
            extrude(context, id + "F1", {"entities" : qUnion([Q0]), "depth" : 25.4 * mm});
        }
        {
            var Q0;
            Q0=makeQuery(id+"F1.opExtrude","CAP_FACE",FACE,{"disambiguationData":[OSD([sQuery(id+"F0.wireOp",EDGE,"E15"),sQuery(id+"F0.wireOp",EDGE,"E16"),sQuery(id+"F0.wireOp",EDGE,"E17"),sQuery(id+"F0.wireOp",EDGE,"E18"),sQuery(id+"F0.wireOp",EDGE,"E19"),sQuery(id+"F0.wireOp",EDGE,"E20"),sQuery(id+"F0.wireOp",EDGE,"E21"),sQuery(id+"F0.wireOp",EDGE,"E22"),sQuery(id+"F0.wireOp",EDGE,"E23"),sQuery(id+"F0.wireOp",EDGE,"E24"),sQuery(id+"F0.wireOp",EDGE,"E25"),sQuery(id+"F0.wireOp",EDGE,"E32"),sQuery(id+"F0.wireOp",EDGE,"E33"),sQuery(id+"F0.wireOp",EDGE,"E34"),sQuery(id+"F0.wireOp",EDGE,"E35"),sQuery(id+"F0.wireOp",EDGE,"E36"),sQuery(id+"F0.wireOp",EDGE,"E37"),sQuery(id+"F0.wireOp",EDGE,"E38"),sQuery(id+"F0.wireOp",EDGE,"E39"),sQuery(id+"F0.wireOp",EDGE,"E40"),sQuery(id+"F0.wireOp",EDGE,"E41"),sQuery(id+"F0.wireOp",EDGE,"E42"),sQuery(id+"F0.wireOp",EDGE,"E43"),sQuery(id+"F0.wireOp",EDGE,"E44"),sQuery(id+"F0.wireOp",EDGE,"E45"),sQuery(id+"F0.wireOp",EDGE,"E46"),sQuery(id+"F0.wireOp",EDGE,"E54"),sQuery(id+"F0.wireOp",EDGE,"E58"),sQuery(id+"F0.wireOp",EDGE,"E59"),sQuery(id+"F0.wireOp",EDGE,"E60"),sQuery(id+"F0.wireOp",EDGE,"E61"),sQuery(id+"F0.wireOp",EDGE,"E62"),sQuery(id+"F0.wireOp",EDGE,"E63"),sQuery(id+"F0.wireOp",EDGE,"E64"),sQuery(id+"F0.wireOp",EDGE,"E119"),sQuery(id+"F0.wireOp",EDGE,"E228"),sQuery(id+"F0.wireOp",EDGE,"E229"),sQuery(id+"F0.wireOp",EDGE,"E230"),sQuery(id+"F0.wireOp",EDGE,"E231"),sQuery(id+"F0.wireOp",EDGE,"E232"),sQuery(id+"F0.wireOp",EDGE,"E233"),sQuery(id+"F0.wireOp",EDGE,"E234"),sQuery(id+"F0.wireOp",EDGE,"E236"),sQuery(id+"F0.wireOp",EDGE,"E237"),sQuery(id+"F0.wireOp",EDGE,"E238"),sQuery(id+"F0.wireOp",EDGE,"E239"),sQuery(id+"F0.wireOp",EDGE,"E240"),sQuery(id+"F0.wireOp",EDGE,"E241")])],"isStart":false});
            var sketch = newSketch(context, id + "F2", { "sketchPlane" : qUnion([Q0])});
            skLineSegment(sketch, "E346", {"start": v(21.62, -14.6) * mm, "end": v(31.15, -10.5) * mm});
            skLineSegment(sketch, "E347", {"start": v(18.9, 2.44) * mm, "end": v(9.54, -3.73) * mm});
            skLineSegment(sketch, "E348", {"start": v(9.54, -3.73) * mm, "end": v(-3.78, -9.66) * mm});
            skLineSegment(sketch, "E349", {"start": v(-3.78, -9.66) * mm, "end": v(-15.27, -0.99) * mm});
            skLineSegment(sketch, "E350", {"start": v(-15.27, -0.99) * mm, "end": v(-25.4, 9.67) * mm});
            skLineSegment(sketch, "E351", {"start": v(-25.4, 9.67) * mm, "end": v(-25.4, 14.23) * mm});
            skLineSegment(sketch, "E352", {"start": v(-25.4, 14.23) * mm, "end": v(-27, 19.1) * mm});
            skLineSegment(sketch, "E353", {"start": v(-27, 19.1) * mm, "end": v(-27.75, 20.17) * mm});
            skLineSegment(sketch, "E354", {"start": v(-27.75, 20.17) * mm, "end": v(-27.75, 18.57) * mm});
            skLineSegment(sketch, "E355", {"start": v(-27.75, 18.57) * mm, "end": v(-29.35, 20.47) * mm});
            skLineSegment(sketch, "E356", {"start": v(-29.35, 20.47) * mm, "end": v(-30.26, 21.57) * mm});
            skLineSegment(sketch, "E357", {"start": v(-30.26, 21.57) * mm, "end": v(-36.24, 27.23) * mm});
            skLineSegment(sketch, "E358", {"start": v(-36.24, 27.23) * mm, "end": v(-32.98, 23.47) * mm});
            skLineSegment(sketch, "E359", {"start": v(-32.98, 23.47) * mm, "end": v(-29.7, 17.68) * mm});
            skLineSegment(sketch, "E360", {"start": v(-38.8, 26.03) * mm, "end": v(-35.14, 16.38) * mm});
            skLineSegment(sketch, "E361", {"start": v(-35.14, 16.38) * mm, "end": v(-38.93, 24.2) * mm});
            skLineSegment(sketch, "E362", {"start": v(-40.16, 23.88) * mm, "end": v(-39.28, 20.68) * mm});
            skLineSegment(sketch, "E363", {"start": v(-23.4, -37.63) * mm, "end": v(-43.14, -58.47) * mm});
            skLineSegment(sketch, "E364", {"start": v(-43.14, -58.47) * mm, "end": v(-22.84, -58.47) * mm});
            skLineSegment(sketch, "E365", {"start": v(-22.84, -58.47) * mm, "end": v(-12.19, -47.52) * mm});
            skLineSegment(sketch, "E366", {"start": v(-12.19, -47.52) * mm, "end": v(-5.82, -50.35) * mm});
            skLineSegment(sketch, "E367", {"start": v(-5.82, -50.35) * mm, "end": v(-4.53, -58.2) * mm});
            skLineSegment(sketch, "E368", {"start": v(-4.53, -58.2) * mm, "end": v(10.95, -58.2) * mm});
            skLineSegment(sketch, "E369", {"start": v(10.95, -58.2) * mm, "end": v(10.95, -50.86) * mm});
            skLineSegment(sketch, "E370", {"start": v(16.39, -43) * mm, "end": v(-15.3, -31.13) * mm});
            skLineSegment(sketch, "E371", {"start": v(-15.3, -31.13) * mm, "end": v(-21.1, -28.85) * mm});
            skLineSegment(sketch, "E372", {"start": v(-21.1, -28.85) * mm, "end": v(-21.95, -32.74) * mm});
            skLineSegment(sketch, "E373", {"start": v(-17.58, 11) * mm, "end": v(-14.8, 9.96) * mm});
            skLineSegment(sketch, "E374", {"start": v(14.92, 7.25) * mm, "end": v(14.06, 9.96) * mm});
            skLineSegment(sketch, "E375", {"start": v(14.06, 9.96) * mm, "end": v(12.46, 11.18) * mm});
            skLineSegment(sketch, "E376", {"start": v(12.46, 11.18) * mm, "end": v(9.14, 12.66) * mm});
            skLineSegment(sketch, "E377", {"start": v(-4.32, 2.74) * mm, "end": v(-4.32, 0) * mm});
            skLineSegment(sketch, "E378", {"start": v(-4.32, 0) * mm, "end": v(-3.46, -4.59) * mm});
            skLineSegment(sketch, "E379", {"start": v(-3.46, -4.59) * mm, "end": v(-3.78, -9.66) * mm});
            skLineSegment(sketch, "E380", {"start": v(-28.44, 1.37) * mm, "end": v(-28.44, -16.24) * mm});
            skPoint(sketch, "E380.startSnap0", {"position": v(-4.32, 1.37) * mm});
            skLineSegment(sketch, "E381", {"start": v(-28.44, -16.24) * mm, "end": v(-24.26, -4.9) * mm});
            skLineSegment(sketch, "E382", {"start": v(-28.44, -16.24) * mm, "end": v(-27.7, -30.02) * mm});
            skLineSegment(sketch, "E383", {"start": v(8.64, 21.8) * mm, "end": v(11.53, 28.13) * mm});
            skLineSegment(sketch, "E384", {"start": v(11.53, 28.13) * mm, "end": v(13.85, 34.63) * mm});
            skLineSegment(sketch, "E385", {"start": v(13.85, 34.63) * mm, "end": v(12.65, 39.52) * mm});
            skLineSegment(sketch, "E386", {"start": v(0, 49.97) * mm, "end": v(3.42, 48.85) * mm});
            skLineSegment(sketch, "E387", {"start": v(3.42, 48.85) * mm, "end": v(6.6, 46.98) * mm});
            skLineSegment(sketch, "E388", {"start": v(6.6, 46.98) * mm, "end": v(9.58, 43.9) * mm});
            skLineSegment(sketch, "E389", {"start": v(9.58, 43.9) * mm, "end": v(12.65, 39.52) * mm});
            skLineSegment(sketch, "E390", {"start": v(6.6, 46.98) * mm, "end": v(6.6, 48.85) * mm});
            skLineSegment(sketch, "E391", {"start": v(6.6, 48.85) * mm, "end": v(3.6, 51.37) * mm});
            skLineSegment(sketch, "E392", {"start": v(3.6, 51.37) * mm, "end": v(1.92, 52.2) * mm});
            skLineSegment(sketch, "E393", {"start": v(1.92, 52.2) * mm, "end": v(0, 49.97) * mm});
            skLineSegment(sketch, "E394", {"start": v(-12.48, 22.8) * mm, "end": v(-14.1, 23.24) * mm});
            skLineSegment(sketch, "E395", {"start": v(-14.1, 23.24) * mm, "end": v(-15.86, 22.02) * mm});
            skLineSegment(sketch, "E396", {"start": v(-15.86, 22.02) * mm, "end": v(-15.42, 20.85) * mm});
            skLineSegment(sketch, "E397", {"start": v(-15.42, 20.85) * mm, "end": v(-14.1, 20.85) * mm});
            skLineSegment(sketch, "E398", {"start": v(-14.1, 20.85) * mm, "end": v(-12.52, 21.8) * mm});
            skLineSegment(sketch, "E399", {"start": v(-12.52, 21.8) * mm, "end": v(-12.48, 22.8) * mm});
            skLineSegment(sketch, "E400", {"start": v(-13.51, 24.3) * mm, "end": v(-12.45, 23.64) * mm});
            skLineSegment(sketch, "E401", {"start": v(-12.45, 23.64) * mm, "end": v(-12.26, 22.5) * mm});
            skLineSegment(sketch, "E402", {"start": v(-12.26, 22.5) * mm, "end": v(-12.48, 20.26) * mm});
            skLineSegment(sketch, "E403", {"start": v(-12.48, 20.26) * mm, "end": v(-12.7, 18.02) * mm});
            skLineSegment(sketch, "E404", {"start": v(-12.7, 18.02) * mm, "end": v(-12.85, 16.95) * mm});
            skLineSegment(sketch, "E405", {"start": v(-12.85, 16.95) * mm, "end": v(-12.2, 15.93) * mm});
            skLineSegment(sketch, "E406", {"start": v(-12.2, 15.93) * mm, "end": v(-11.27, 15.34) * mm});
            skLineSegment(sketch, "E407", {"start": v(-11.27, 15.34) * mm, "end": v(-10.28, 15.34) * mm});
            skLineSegment(sketch, "E408", {"start": v(-7.86, 17.76) * mm, "end": v(-7.3, 17.21) * mm});
            skLineSegment(sketch, "E409", {"start": v(-7.3, 17.21) * mm, "end": v(-7.67, 16.4) * mm});
            skLineSegment(sketch, "E410", {"start": v(-10.07, 16.18) * mm, "end": v(-9.34, 16.4) * mm});
            skLineSegment(sketch, "E411", {"start": v(-9.34, 16.4) * mm, "end": v(-8.73, 16.31) * mm});
            skLineSegment(sketch, "E412", {"start": v(-8.73, 16.31) * mm, "end": v(-8.55, 16.58) * mm});
            skLineSegment(sketch, "E413", {"start": v(-8.55, 16.58) * mm, "end": v(-8.94, 16.83) * mm});
            skLineSegment(sketch, "E414", {"start": v(-8.94, 16.83) * mm, "end": v(-9.5, 16.85) * mm});
            skLineSegment(sketch, "E415", {"start": v(-9.5, 16.85) * mm, "end": v(-10.07, 16.18) * mm});
            skLineSegment(sketch, "E416", {"start": v(-9.63, 11.74) * mm, "end": v(-8.83, 12.6) * mm});
            skLineSegment(sketch, "E417", {"start": v(-8.83, 12.6) * mm, "end": v(-7.53, 12.97) * mm});
            skLineSegment(sketch, "E418", {"start": v(-7.53, 12.97) * mm, "end": v(-4.8, 13.23) * mm});
            skLineSegment(sketch, "E419", {"start": v(-4.8, 13.23) * mm, "end": v(-5, 12.4) * mm});
            skLineSegment(sketch, "E420", {"start": v(-5, 12.4) * mm, "end": v(-6.36, 11.14) * mm});
            skLineSegment(sketch, "E421", {"start": v(-6.36, 11.14) * mm, "end": v(-8.52, 10.56) * mm});
            skLineSegment(sketch, "E422", {"start": v(-8.52, 10.56) * mm, "end": v(-9.63, 11.74) * mm});
            skLineSegment(sketch, "E423", {"start": v(-4.33, 13.51) * mm, "end": v(-6.3, 14.37) * mm});
            skLineSegment(sketch, "E424", {"start": v(-6.3, 14.37) * mm, "end": v(-8.17, 14.3) * mm});
            skLineSegment(sketch, "E425", {"start": v(-8.17, 14.3) * mm, "end": v(-9.37, 13.74) * mm});
            skLineSegment(sketch, "E426", {"start": v(-9.37, 13.74) * mm, "end": v(-10.07, 13.39) * mm});
            skLineSegment(sketch, "E427", {"start": v(-10.07, 13.39) * mm, "end": v(-10.52, 12.66) * mm});
            skLineSegment(sketch, "E428", {"start": v(-10.52, 12.66) * mm, "end": v(-10.39, 12) * mm});
            skLineSegment(sketch, "E429", {"start": v(-10.39, 12) * mm, "end": v(-9.98, 11.45) * mm});
            skLineSegment(sketch, "E430", {"start": v(-9.98, 11.45) * mm, "end": v(-8.52, 10.56) * mm});
            skLineSegment(sketch, "E431", {"start": v(-4.33, 13.51) * mm, "end": v(-3.95, 13.51) * mm});
            skLineSegment(sketch, "E432", {"start": v(-3.95, 13.51) * mm, "end": v(-3.73, 12.88) * mm});
            skLineSegment(sketch, "E433", {"start": v(-3.73, 12.88) * mm, "end": v(-4.43, 10.91) * mm});
            skLineSegment(sketch, "E434", {"start": v(-4.43, 10.91) * mm, "end": v(-5.1, 10) * mm});
            skLineSegment(sketch, "E435", {"start": v(-5.1, 10) * mm, "end": v(-6.49, 9.17) * mm});
            skLineSegment(sketch, "E436", {"start": v(-6.49, 9.17) * mm, "end": v(-7.98, 8.85) * mm});
            skLineSegment(sketch, "E437", {"start": v(-7.98, 8.85) * mm, "end": v(-8.77, 9.26) * mm});
            skLineSegment(sketch, "E438", {"start": v(-8.77, 9.26) * mm, "end": v(-9.22, 10.06) * mm});
            skLineSegment(sketch, "E439", {"start": v(-9.22, 10.06) * mm, "end": v(-8.52, 10.56) * mm});
            skLineSegment(sketch, "E440", {"start": v(-9.23, 12.17) * mm, "end": v(-8.58, 11.7) * mm});
            skLineSegment(sketch, "E441", {"start": v(-8.58, 11.7) * mm, "end": v(-7.47, 11.93) * mm});
            skLineSegment(sketch, "E442", {"start": v(-7.47, 11.93) * mm, "end": v(-6.46, 12.44) * mm});
            skLineSegment(sketch, "E443", {"start": v(-6.46, 12.44) * mm, "end": v(-6.17, 13.1) * mm});
            skLineSegment(sketch, "E444", {"start": v(-6.17, 13.1) * mm, "end": v(-4.8, 13.23) * mm});
            skSolve(sketch);
        }
        {
            var Q0;
            Q0=makeQuery(id+"F2.imprint","IMPRINT",FACE,{"disambiguationData":[TD([[makeQuery(id+"F2.imprint","IMPRINT",EDGE,{"derivedFrom":sQuery(id+"F2.wireOp",EDGE,"E386")}),1.0]])]});
            var Q1;
            Q1=makeQuery(id+"F2.imprint","IMPRINT",FACE,{"disambiguationData":[TD([[makeQuery(id+"F2.imprint","IMPRINT",EDGE,{"derivedFrom":sQuery(id+"F2.wireOp",EDGE,"E410")}),1.0]])]});
            var Q2;
            {var subQ2=sQuery(id+"F2.wireOp",EDGE,"E367");Q2=makeQuery(id+"F2.imprint","IMPRINT",FACE,{"disambiguationData":[TD([[makeQuery(id+"F2.imprint","IMPRINT",EDGE,{"derivedFrom":subQ2}),1.0]])]});}
            var Q3;
            Q3=makeQuery(id+"F2.imprint","IMPRINT",FACE,{"disambiguationData":[TD([[makeQuery(id+"F2.imprint","IMPRINT",EDGE,{"derivedFrom":sQuery(id+"F2.wireOp",EDGE,"E363")}),1.0]])]});
            extrude(context, id + "F3", {"entities" : qUnion([Q0, Q1, Q2, Q3]), "operationType" : NewBodyOperationType.ADD, "depth" : 25.4 * mm});
        }
    });
